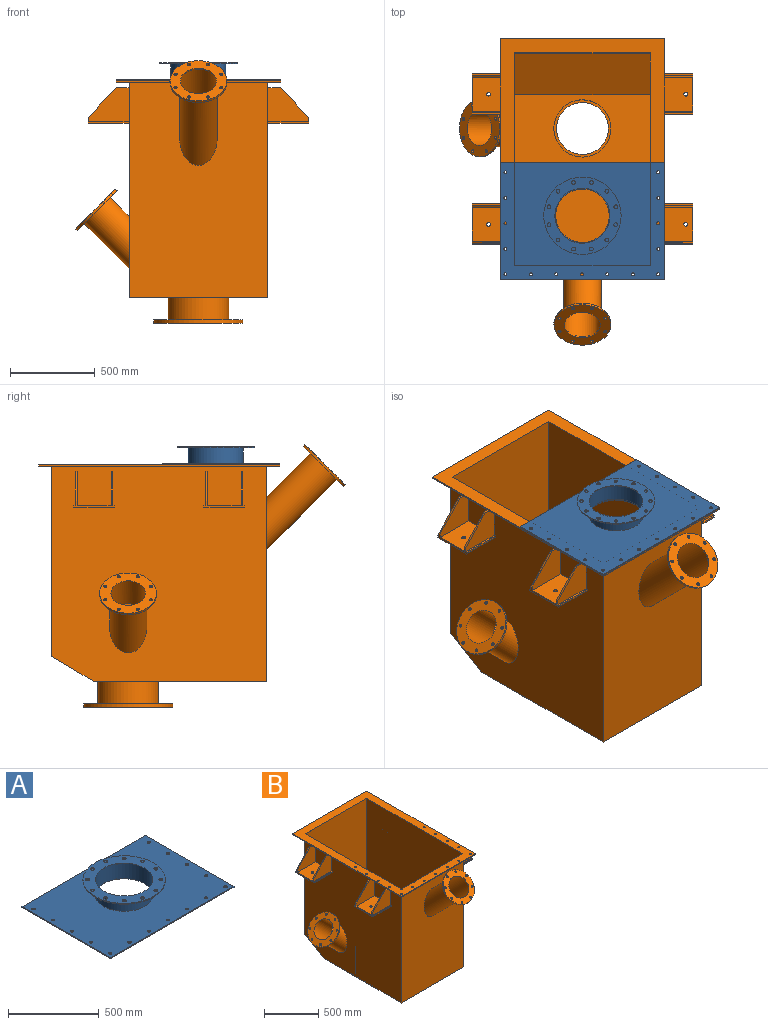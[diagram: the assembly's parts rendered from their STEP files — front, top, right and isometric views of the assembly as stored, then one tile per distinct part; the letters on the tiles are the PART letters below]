
ASSEMBLY  parts=2 mates=1
PART A: 38 faces, bbox 966x690x106 mm
  f0: cylinder r=161.9mm len=323.8mm, axis (0,0,-1), area 95621.3mm2, adj f20,f35
  f1: plane 966x6mm, normal (0,1,0), area 5796mm2, adj f2,f18,f20,f21
  f2: plane 690x6mm, normal (-1,0,0), area 4140mm2, adj f1,f3,f20,f21
  f3: plane 966x6mm, normal (0,-1,0), area 5796mm2, adj f2,f18,f20,f21
  f4: cylinder r=9mm len=18mm, axis (0,0,-1), area 339.3mm2, adj f20,f21
  f5: cylinder r=9mm len=18mm, axis (0,0,-1), area 339.3mm2, adj f20,f21
  f6: cylinder r=9mm len=18mm, axis (0,0,-1), area 339.3mm2, adj f20,f21
  f7: cylinder r=9mm len=18mm, axis (0,0,-1), area 339.3mm2, adj f20,f21
  f8: cylinder r=9mm len=18mm, axis (0,0,-1), area 339.3mm2, adj f20,f21
  f9: cylinder r=9mm len=18mm, axis (0,0,-1), area 339.3mm2, adj f20,f21
  f10: cylinder r=9mm len=18mm, axis (0,0,-1), area 339.3mm2, adj f20,f21
  f11: cylinder r=9mm len=18mm, axis (0,0,-1), area 339.3mm2, adj f20,f21
  f12: cylinder r=9mm len=18mm, axis (0,0,-1), area 339.3mm2, adj f20,f21
  f13: cylinder r=9mm len=18mm, axis (0,0,-1), area 339.3mm2, adj f20,f21
  f14: cylinder r=9mm len=18mm, axis (0,0,-1), area 339.3mm2, adj f20,f21
  f15: cylinder r=9mm len=18mm, axis (0,0,-1), area 339.3mm2, adj f20,f21
  f16: cylinder r=9mm len=18mm, axis (0,0,-1), area 339.3mm2, adj f20,f21
  f17: cylinder r=9mm len=18mm, axis (0,0,-1), area 339.3mm2, adj f20,f21
  f18: plane 690x6mm, normal (1,0,0), area 4140mm2, adj f1,f3,f20,f21
  f19: cylinder r=9mm len=18mm, axis (0,0,-1), area 339.3mm2, adj f20,f21
  f20: plane 966x690mm, normal (0,0,1), area 580376.8mm2, adj f0,f1,f2,f3,f4,f5,f6,f7
  f21: plane 966x690mm, normal (0,0,-1), area 584960mm2, adj f1,f2,f3,f4,f5,f6,f7,f8
  f22: cylinder r=11mm len=22mm, axis (0,0,1), area 414.7mm2, adj f35,f37
  f23: cylinder r=11mm len=22mm, axis (0,0,1), area 414.7mm2, adj f35,f37
  f24: cylinder r=11mm len=22mm, axis (0,0,1), area 414.7mm2, adj f35,f37
  f25: cylinder r=11mm len=22mm, axis (0,0,1), area 414.7mm2, adj f35,f37
  f26: cylinder r=11mm len=22mm, axis (0,0,1), area 414.7mm2, adj f35,f37
  f27: cylinder r=11mm len=22mm, axis (0,0,1), area 414.7mm2, adj f35,f37
  f28: cylinder r=11mm len=22mm, axis (0,0,1), area 414.7mm2, adj f35,f37
  f29: cylinder r=11mm len=22mm, axis (0,0,1), area 414.7mm2, adj f35,f37
  f30: cylinder r=11mm len=22mm, axis (0,0,1), area 414.7mm2, adj f35,f37
  f31: cylinder r=11mm len=22mm, axis (0,0,1), area 414.7mm2, adj f35,f37
  f32: cylinder r=11mm len=22mm, axis (0,0,1), area 414.7mm2, adj f35,f37
  f33: cylinder r=11mm len=22mm, axis (0,0,1), area 414.7mm2, adj f35,f37
  f34: cylinder r=227.5mm len=455mm, axis (0,0,1), area 8576.5mm2, adj f35,f37
  f35: plane 455x455mm, normal (0,0,-1), area 75689.3mm2, adj f0,f22,f23,f24,f25,f26,f27,f28
  f36: cylinder r=157.33mm len=314.66mm, axis (0,0,-1), area 104784.6mm2, adj f21,f37
  f37: plane 455x455mm, normal (0,0,1), area 80272.5mm2, adj f22,f23,f24,f25,f26,f27,f28,f29
PART B: 146 faces, bbox 1417.8x1848.1x1590.9 mm
  f0: plane 1269x1266mm, normal (-1,0,0), area 1521684.1mm2, adj f4,f6,f8,f9,f35,f99,f100,f101
  f1: cylinder r=109.55mm len=565.81mm, axis (0,-0.71,0.71), area 324565.8mm2, adj f6,f48
  f2: plane 800x415.78mm, normal (0,0,1), area 243673.8mm2, adj f3,f11,f14,f15,f37
  f3: plane 1269x1250mm, normal (-1,0,0), area 1562857.6mm2, adj f2,f7,f10,f12,f13,f14,f36,f37
  f4: plane 1119x816mm, normal (0,1,0), area 913104mm2, adj f0,f5,f9,f35
  f5: plane 1269x1266mm, normal (1,0,0), area 1575004mm2, adj f4,f6,f8,f9,f35,f69,f70,f71
  f6: plane 1315.08x862.08mm, normal (0,-1,0), area 982184.1mm2, adj f0,f1,f5,f8,f35
  f7: plane 1416x966mm, normal (0,0,1), area 364039mm2, adj f3,f10,f11,f12,f16,f17,f18,f19
  f8: plane 1016x816mm, normal (0,0,-1), area 729741.3mm2, adj f0,f5,f6,f9,f51
  f9: plane 816x250mm, normal (0,0.51,-0.86), area 237902.8mm2, adj f0,f4,f5,f8
  f10: plane 1122.47x800mm, normal (0,-1,0), area 897976.4mm2, adj f3,f7,f11,f14
  f11: plane 1269x1250mm, normal (1,0,0), area 1517203.1mm2, adj f2,f7,f10,f12,f13,f14,f36,f37
  f12: plane 1313.49x844.49mm, normal (0,1,0), area 965477.4mm2, adj f3,f7,f11,f13,f50
  f13: plane 800x580mm, normal (0,0,1), area 464000mm2, adj f3,f11,f12,f36
  f14: plane 800x244.22mm, normal (0,-0.51,0.86), area 227841.8mm2, adj f2,f3,f10,f11
  f15: cylinder r=168.27mm len=336.54mm, axis (0,0,-1), area 146960.8mm2, adj f2,f52
  f16: plane 1416x8mm, normal (1,0,0), area 11328mm2, adj f7,f17,f33,f35
  f17: plane 966x8mm, normal (0,1,0), area 7728mm2, adj f7,f16,f18,f35
  f18: plane 1416x8mm, normal (-1,0,0), area 11328mm2, adj f7,f17,f33,f35
  f19: cylinder r=9mm len=18mm, axis (0,0,1), area 452.4mm2, adj f7,f35
  f20: cylinder r=9mm len=18mm, axis (0,0,1), area 452.4mm2, adj f7,f35
  f21: cylinder r=9mm len=18mm, axis (0,0,1), area 452.4mm2, adj f7,f35
  f22: cylinder r=9mm len=18mm, axis (0,0,1), area 452.4mm2, adj f7,f35
  f23: cylinder r=9mm len=18mm, axis (0,0,1), area 452.4mm2, adj f7,f35
  f24: cylinder r=9mm len=18mm, axis (0,0,1), area 452.4mm2, adj f7,f35
  f25: cylinder r=9mm len=18mm, axis (0,0,1), area 452.4mm2, adj f7,f35
  f26: cylinder r=9mm len=18mm, axis (0,0,1), area 452.4mm2, adj f7,f35
  f27: cylinder r=9mm len=18mm, axis (0,0,1), area 452.4mm2, adj f7,f35
  f28: cylinder r=9mm len=18mm, axis (0,0,1), area 452.4mm2, adj f7,f35
  f29: cylinder r=9mm len=18mm, axis (0,0,1), area 452.4mm2, adj f7,f35
  f30: cylinder r=9mm len=18mm, axis (0,0,1), area 452.4mm2, adj f7,f35
  f31: cylinder r=9mm len=18mm, axis (0,0,1), area 452.4mm2, adj f7,f35
  f32: cylinder r=9mm len=18mm, axis (0,0,1), area 452.4mm2, adj f7,f35
  f33: plane 966x8mm, normal (0,-1,0), area 7728mm2, adj f7,f16,f18,f35
  f34: cylinder r=9mm len=18mm, axis (0,0,1), area 452.4mm2, adj f7,f35
  f35: plane 1416x966mm, normal (0,0,-1), area 330983mm2, adj f0,f4,f5,f6,f16,f17,f18,f19
  f36: plane 800x550mm, normal (0,-1,0), area 440000mm2, adj f3,f11,f13,f38
  f37: plane 800x550mm, normal (0,1,0), area 440000mm2, adj f2,f3,f11,f38
  f38: plane 800x10mm, normal (0,0,1), area 8000mm2, adj f3,f11,f36,f37
  f39: cylinder r=9mm len=21.92mm, axis (0,-0.71,0.71), area 735.1mm2, adj f48,f49
  f40: cylinder r=9mm len=21.92mm, axis (0,-0.71,0.71), area 735.1mm2, adj f48,f49
  f41: cylinder r=9mm len=21.92mm, axis (0,-0.71,0.71), area 735.1mm2, adj f48,f49
  f42: cylinder r=9mm len=21.92mm, axis (0,-0.71,0.71), area 735.1mm2, adj f48,f49
  f43: cylinder r=9mm len=21.92mm, axis (0,-0.71,0.71), area 735.1mm2, adj f48,f49
  f44: cylinder r=9mm len=21.92mm, axis (0,-0.71,0.71), area 735.1mm2, adj f48,f49
  f45: cylinder r=9mm len=21.92mm, axis (0,-0.71,0.71), area 735.1mm2, adj f48,f49
  f46: cylinder r=9mm len=21.92mm, axis (0,-0.71,0.71), area 735.1mm2, adj f48,f49
  f47: cylinder r=167.5mm len=335mm, axis (0,-0.71,0.71), area 13681.6mm2, adj f48,f49
  f48: plane 335x236.88mm, normal (0,0.71,-0.71), area 48402.7mm2, adj f1,f39,f40,f41,f42,f43,f44,f45
  f49: plane 335x236.88mm, normal (0,-0.71,0.71), area 50946.3mm2, adj f39,f40,f41,f42,f43,f44,f45,f46
  f50: cylinder r=105.79mm len=575.03mm, axis (0,-0.71,0.71), area 329587.2mm2, adj f12,f49
  f51: cylinder r=177.8mm len=355.6mm, axis (0,0,1), area 146346.7mm2, adj f8,f68
  f52: plane 336.54x336.54mm, normal (0,0,1), area 16016.4mm2, adj f15,f65
  f53: cylinder r=11mm len=22mm, axis (0,0,1), area 1313.2mm2, adj f67,f68
  f54: cylinder r=11mm len=22mm, axis (0,0,1), area 1313.2mm2, adj f67,f68
  f55: cylinder r=11mm len=22mm, axis (0,0,1), area 1313.2mm2, adj f67,f68
  f56: cylinder r=11mm len=22mm, axis (0,0,1), area 1313.2mm2, adj f67,f68
  f57: cylinder r=11mm len=22mm, axis (0,0,1), area 1313.2mm2, adj f67,f68
  f58: cylinder r=11mm len=22mm, axis (0,0,1), area 1313.2mm2, adj f67,f68
  f59: cylinder r=11mm len=22mm, axis (0,0,1), area 1313.2mm2, adj f67,f68
  f60: cylinder r=11mm len=22mm, axis (0,0,1), area 1313.2mm2, adj f67,f68
  f61: cylinder r=11mm len=22mm, axis (0,0,1), area 1313.2mm2, adj f67,f68
  f62: cylinder r=11mm len=22mm, axis (0,0,1), area 1313.2mm2, adj f67,f68
  f63: cylinder r=11mm len=22mm, axis (0,0,1), area 1313.2mm2, adj f67,f68
  f64: cylinder r=11mm len=22mm, axis (0,0,1), area 1313.2mm2, adj f67,f68
  f65: cylinder r=152.37mm len=304.74mm, axis (0,0,1), area 18190mm2, adj f52,f67
  f66: cylinder r=262.5mm len=525mm, axis (0,0,1), area 31337.4mm2, adj f67,f68
  f67: plane 525x525mm, normal (0,0,-1), area 138976.6mm2, adj f53,f54,f55,f56,f57,f58,f59,f60
  f68: plane 525x525mm, normal (0,0,1), area 112599.1mm2, adj f51,f53,f54,f55,f56,f57,f58,f59
  f69: plane 240x200mm, normal (0,-1,0), area 33562.5mm2, adj f5,f74,f75,f76,f82
  f70: plane 75x10mm, normal (0,0,1), area 750mm2, adj f5,f71,f72,f83
  f71: plane 240x200mm, normal (0,1,0), area 33562.5mm2, adj f5,f70,f74,f80,f83
  f72: plane 240x200mm, normal (0,-1,0), area 33562.5mm2, adj f5,f70,f74,f81,f83
  f73: plane 240x200mm, normal (0,1,0), area 33562.5mm2, adj f5,f74,f75,f81,f82
  f74: plane 240x35mm, normal (1,0,0), area 2900mm2, adj f69,f71,f72,f73,f76,f77,f78,f79
  f75: plane 75x10mm, normal (0,0,1), area 750mm2, adj f5,f69,f73,f82
  f76: plane 240x10mm, normal (0,0,1), area 2400mm2, adj f5,f69,f74,f77
  f77: plane 240x10mm, normal (0,-1,0), area 2400mm2, adj f5,f74,f76,f78
  f78: plane 240x240mm, normal (0,0,-1), area 57219.9mm2, adj f5,f74,f77,f79,f132
  f79: plane 240x10mm, normal (0,1,0), area 2400mm2, adj f5,f74,f78,f80
  f80: plane 240x10mm, normal (0,0,1), area 2400mm2, adj f5,f71,f74,f79
  f81: plane 240x200mm, normal (0,0,1), area 47619.9mm2, adj f5,f72,f73,f74,f132
  f82: plane 175x165mm, normal (0.73,0,0.69), area 2405.2mm2, adj f69,f73,f74,f75
  f83: plane 175x165mm, normal (0.73,0,0.69), area 2405.2mm2, adj f70,f71,f72,f74
  f84: plane 75x10mm, normal (0,0,1), area 750mm2, adj f5,f85,f86,f98
  f85: plane 240x200mm, normal (0,1,0), area 33562.5mm2, adj f5,f84,f89,f90,f98
  f86: plane 240x200mm, normal (0,-1,0), area 33562.5mm2, adj f5,f84,f89,f91,f98
  f87: plane 240x200mm, normal (0,1,0), area 33562.5mm2, adj f5,f89,f91,f92,f97
  f88: plane 240x200mm, normal (0,-1,0), area 33562.5mm2, adj f5,f89,f92,f93,f97
  f89: plane 240x35mm, normal (1,0,0), area 2900mm2, adj f85,f86,f87,f88,f90,f91,f93,f94
  f90: plane 240x10mm, normal (0,0,1), area 2400mm2, adj f5,f85,f89,f96
  f91: plane 240x200mm, normal (0,0,1), area 47619.9mm2, adj f5,f86,f87,f89,f131
  f92: plane 75x10mm, normal (0,0,1), area 750mm2, adj f5,f87,f88,f97
  f93: plane 240x10mm, normal (0,0,1), area 2400mm2, adj f5,f88,f89,f94
  f94: plane 240x10mm, normal (0,-1,0), area 2400mm2, adj f5,f89,f93,f95
  f95: plane 240x240mm, normal (0,0,-1), area 57219.9mm2, adj f5,f89,f94,f96,f131
  f96: plane 240x10mm, normal (0,1,0), area 2400mm2, adj f5,f89,f90,f95
  f97: plane 175x165mm, normal (0.73,0,0.69), area 2405.2mm2, adj f87,f88,f89,f92
  f98: plane 175x165mm, normal (0.73,0,0.69), area 2405.2mm2, adj f84,f85,f86,f89
  f99: plane 240x200mm, normal (0,-1,0), area 33562.5mm2, adj f0,f104,f105,f106,f112
  f100: plane 75x10mm, normal (0,0,1), area 750mm2, adj f0,f101,f102,f113
  f101: plane 240x200mm, normal (0,1,0), area 33562.5mm2, adj f0,f100,f104,f110,f113
  f102: plane 240x200mm, normal (0,-1,0), area 33562.5mm2, adj f0,f100,f104,f111,f113
  f103: plane 240x200mm, normal (0,1,0), area 33562.5mm2, adj f0,f104,f105,f111,f112
  f104: plane 240x35mm, normal (-1,0,0), area 2900mm2, adj f99,f101,f102,f103,f106,f107,f108,f109
  f105: plane 75x10mm, normal (0,0,1), area 750mm2, adj f0,f99,f103,f112
  f106: plane 240x10mm, normal (0,0,1), area 2400mm2, adj f0,f99,f104,f107
  f107: plane 240x10mm, normal (0,-1,0), area 2400mm2, adj f0,f104,f106,f108
  f108: plane 240x240mm, normal (0,0,-1), area 57219.9mm2, adj f0,f104,f107,f109,f130
  f109: plane 240x10mm, normal (0,1,0), area 2400mm2, adj f0,f104,f108,f110
  f110: plane 240x10mm, normal (0,0,1), area 2400mm2, adj f0,f101,f104,f109
  f111: plane 240x200mm, normal (0,0,1), area 47619.9mm2, adj f0,f102,f103,f104,f130
  f112: plane 175x165mm, normal (-0.73,0,0.69), area 2405.2mm2, adj f99,f103,f104,f105
  f113: plane 175x165mm, normal (-0.73,0,0.69), area 2405.2mm2, adj f100,f101,f102,f104
  f114: plane 75x10mm, normal (0,0,1), area 750mm2, adj f0,f115,f116,f128
  f115: plane 240x200mm, normal (0,1,0), area 33562.5mm2, adj f0,f114,f119,f120,f128
  f116: plane 240x200mm, normal (0,-1,0), area 33562.5mm2, adj f0,f114,f119,f121,f128
  f117: plane 240x200mm, normal (0,1,0), area 33562.5mm2, adj f0,f119,f121,f122,f127
  f118: plane 240x200mm, normal (0,-1,0), area 33562.5mm2, adj f0,f119,f122,f123,f127
  f119: plane 240x35mm, normal (-1,0,0), area 2900mm2, adj f115,f116,f117,f118,f120,f121,f123,f124
  f120: plane 240x10mm, normal (0,0,1), area 2400mm2, adj f0,f115,f119,f126
  f121: plane 240x200mm, normal (0,0,1), area 47619.9mm2, adj f0,f116,f117,f119,f129
  f122: plane 75x10mm, normal (0,0,1), area 750mm2, adj f0,f117,f118,f127
  f123: plane 240x10mm, normal (0,0,1), area 2400mm2, adj f0,f118,f119,f124
  f124: plane 240x10mm, normal (0,-1,0), area 2400mm2, adj f0,f119,f123,f125
  f125: plane 240x240mm, normal (0,0,-1), area 57219.9mm2, adj f0,f119,f124,f126,f129
  f126: plane 240x10mm, normal (0,1,0), area 2400mm2, adj f0,f119,f120,f125
  f127: plane 175x165mm, normal (-0.73,0,0.69), area 2405.2mm2, adj f117,f118,f119,f122
  f128: plane 175x165mm, normal (-0.73,0,0.69), area 2405.2mm2, adj f114,f115,f116,f119
  f129: cylinder r=11mm len=22mm, axis (0,0,-1), area 691.2mm2, adj f121,f125
  f130: cylinder r=11mm len=22mm, axis (0,0,-1), area 691.2mm2, adj f108,f111
  f131: cylinder r=11mm len=22mm, axis (0,0,-1), area 691.2mm2, adj f91,f95
  f132: cylinder r=11mm len=22mm, axis (0,0,-1), area 691.2mm2, adj f78,f81
  f133: cylinder r=101.37mm len=421.28mm, axis (-0.71,0,0.71), area 184887.1mm2, adj f11,f135
  f134: cylinder r=109.55mm len=421.52mm, axis (-0.71,0,0.71), area 183070.7mm2, adj f0,f145
  f135: plane 335x236.88mm, normal (-0.71,0,0.71), area 53822.9mm2, adj f133,f136,f137,f138,f139,f140,f141,f142
  f136: cylinder r=9mm len=21.92mm, axis (-0.71,0,0.71), area 735.1mm2, adj f135,f145
  f137: cylinder r=9mm len=21.92mm, axis (-0.71,0,0.71), area 735.1mm2, adj f135,f145
  f138: cylinder r=9mm len=21.92mm, axis (-0.71,0,0.71), area 735.1mm2, adj f135,f145
  f139: cylinder r=9mm len=21.92mm, axis (-0.71,0,0.71), area 735.1mm2, adj f135,f145
  f140: cylinder r=9mm len=21.92mm, axis (-0.71,0,0.71), area 735.1mm2, adj f135,f145
  f141: cylinder r=9mm len=21.92mm, axis (-0.71,0,0.71), area 735.1mm2, adj f135,f145
  f142: cylinder r=9mm len=21.92mm, axis (-0.71,0,0.71), area 735.1mm2, adj f135,f145
  f143: cylinder r=9mm len=21.92mm, axis (-0.71,0,0.71), area 735.1mm2, adj f135,f145
  f144: cylinder r=167.5mm len=335mm, axis (-0.71,0,0.71), area 13681.6mm2, adj f135,f145
  f145: plane 335x236.88mm, normal (0.71,0,-0.71), area 48402.7mm2, adj f134,f136,f137,f138,f139,f140,f141,f142
PLACE A t=(-127,5.05,-834.6)mm
PLACE B t=(-127,5.05,-834.6)mm
MATE revolute A.f13 <-> B.f20  axis (0,0,-1) through (-580,-672.95,573.4)mm
